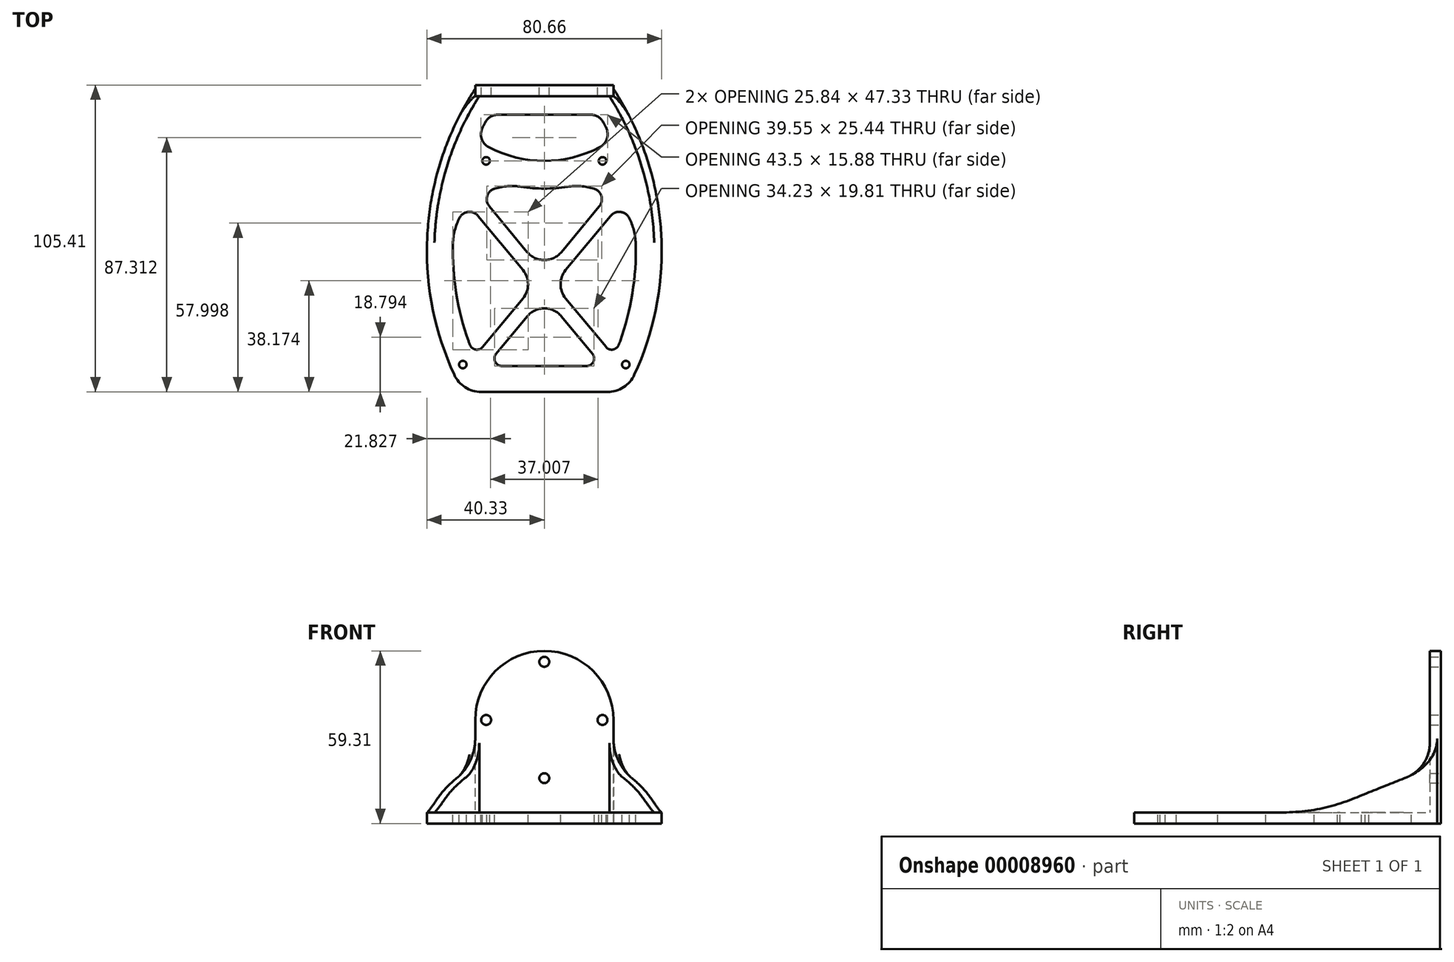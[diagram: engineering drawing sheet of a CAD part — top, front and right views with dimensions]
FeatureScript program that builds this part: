
annotation { "Feature Type Name" : "Feature", "Feature Type Description" : "" }
export const myFeature = defineFeature(function(context is Context, id is Id, definition is map)
    precondition{}
    {
        {
            var Q0;
            Q0=qCreatedBy(makeId("Front.planeOp"),FACE);
            var sketch = newSketch(context, id + "F0", { "sketchPlane" : qUnion([Q0])});
            skCircle(sketch, "E0", {"center": v(0, 19.99) * mm, "radius": 1.7 * mm});
            skCircle(sketch, "E1.1.0", {"center": v(-19.99, 0) * mm, "radius": 1.7 * mm});
            skCircle(sketch, "E1.2.0", {"center": v(0, -19.99) * mm, "radius": 1.7 * mm});
            skCircle(sketch, "E1.3.0", {"center": v(19.99, 0) * mm, "radius": 1.7 * mm});
            skPoint(sketch, "E1.center", {"position": v(0, 0) * mm});
            skArc(sketch, "E2", {"start": v(23.75, 0) * mm, "mid": v(0, 23.75) * mm, "end": v(-23.75, 0) * mm});
            skLineSegment(sketch, "E3.top", {"start": v(-23.75, -31.75) * mm, "end": v(23.75, -31.75) * mm});
            skLineSegment(sketch, "E3.left", {"start": v(-23.75, 0) * mm, "end": v(-23.75, -31.75) * mm});
            skLineSegment(sketch, "E3.right", {"start": v(23.75, 0) * mm, "end": v(23.75, -31.75) * mm});
            skSolve(sketch);
        }
        {
            var Q0;
            Q0=qSketchRegion(id+"F0",true);
            extrude(context, id + "F1", {"entities" : qUnion([Q0]), "depth" : 2.54 * mm});
        }
        {
            var Q0;
            Q0=makeQuery(id+"F1.opExtrude","SWEPT_FACE",FACE,{"disambiguationData":[OSD([sQuery(id+"F0.wireOp",EDGE,"E3.top")])]});
            var sketch = newSketch(context, id + "F2", { "sketchPlane" : qUnion([Q0])});
            skCircle(sketch, "E4", {"center": v(-20, 24.77) * mm, "radius": 1.3 * mm});
            skCircle(sketch, "E5", {"center": v(-28, 94.77) * mm, "radius": 1.3 * mm});
            skLineSegment(sketch, "E6", {"start": v(-20, 24.77) * mm, "end": v(-20, 0) * mm, "construction": true});
            skLineSegment(sketch, "E7", {"start": v(-28, 94.77) * mm, "end": v(-28, 0) * mm, "construction": true});
            skCircle(sketch, "E8.0.MirrorC", {"center": v(20, 24.77) * mm, "radius": 1.3 * mm});
            skCircle(sketch, "E8.1.MirrorC", {"center": v(28, 94.77) * mm, "radius": 1.3 * mm});
            skArc(sketch, "E9", {"start": v(-30.96, 98.24) * mm, "mid": v(-40.06, 48.19) * mm, "end": v(-23.75, 0) * mm});
            skArc(sketch, "E10.0.MirrorCS", {"start": v(30.96, 98.24) * mm, "mid": v(40.06, 48.19) * mm, "end": v(23.75, 0) * mm});
            skLineSegment(sketch, "E11", {"start": v(-21.74, 104.14) * mm, "end": v(21.74, 104.14) * mm});
            skPoint(sketch, "E12.visualSharp", {"position": v(-28, 104.14) * mm});
            skArc(sketch, "E12.filletArc", {"start": v(-21.74, 104.14) * mm, "mid": v(-27.22, 102.54) * mm, "end": v(-30.96, 98.24) * mm});
            skPoint(sketch, "E13.visualSharp", {"position": v(28, 104.14) * mm});
            skArc(sketch, "E13.filletArc", {"start": v(30.96, 98.24) * mm, "mid": v(27.22, 102.54) * mm, "end": v(21.74, 104.14) * mm});
            skLineSegment(sketch, "E14", {"start": v(-23.75, 0) * mm, "end": v(23.75, 0) * mm});
            skArc(sketch, "E15.0", {"start": v(-26.04, 86.82) * mm, "mid": v(-30.28, 70.26) * mm, "end": v(-31.41, 53.2) * mm});
            skLineSegment(sketch, "E15.1", {"start": v(-14.08, 95.25) * mm, "end": v(14.08, 95.25) * mm});
            skArc(sketch, "E15.2", {"start": v(26.04, 86.82) * mm, "mid": v(30.28, 70.26) * mm, "end": v(31.41, 53.2) * mm});
            skLineSegment(sketch, "E15.3", {"start": v(-15.83, 8.89) * mm, "end": v(15.83, 8.89) * mm});
            skArc(sketch, "E16", {"start": v(7.93, 33.67) * mm, "mid": v(0, 34.3) * mm, "end": v(-7.93, 33.67) * mm});
            skArc(sketch, "E17", {"start": v(19.03, 20.12) * mm, "mid": v(0, 24.77) * mm, "end": v(-19.03, 20.12) * mm});
            skArc(sketch, "E18.trimOffspring", {"start": v(21.2, 13.29) * mm, "mid": v(20.76, 12.42) * mm, "end": v(20.3, 11.55) * mm});
            skArc(sketch, "E19.trimOffspring", {"start": v(-21.2, 13.29) * mm, "mid": v(-20.76, 12.42) * mm, "end": v(-20.3, 11.55) * mm});
            skPoint(sketch, "E20.visualSharp", {"position": v(-26.8, 26.65) * mm});
            skArc(sketch, "E20.filletArc", {"start": v(-31.41, 53.2) * mm, "mid": v(-30.77, 48.64) * mm, "end": v(-29.1, 44.33) * mm});
            skPoint(sketch, "E21.visualSharp", {"position": v(26.8, 26.65) * mm});
            skArc(sketch, "E21.filletArc", {"start": v(7.93, 33.67) * mm, "mid": v(12.55, 33.47) * mm, "end": v(17.1, 34.32) * mm});
            skPoint(sketch, "E22.visualSharp", {"position": v(18.8, 8.89) * mm});
            skArc(sketch, "E22.filletArc", {"start": v(15.83, 8.89) * mm, "mid": v(18.43, 9.6) * mm, "end": v(20.3, 11.55) * mm});
            skPoint(sketch, "E23.visualSharp", {"position": v(-18.8, 8.89) * mm});
            skArc(sketch, "E23.filletArc", {"start": v(-20.3, 11.55) * mm, "mid": v(-18.43, 9.6) * mm, "end": v(-15.83, 8.89) * mm});
            skPoint(sketch, "E24.visualSharp", {"position": v(-23.27, 17.58) * mm});
            skArc(sketch, "E24.filletArc", {"start": v(-19.03, 20.12) * mm, "mid": v(-21.53, 17.15) * mm, "end": v(-21.2, 13.29) * mm});
            skPoint(sketch, "E25.visualSharp", {"position": v(23.27, 17.58) * mm});
            skArc(sketch, "E25.filletArc", {"start": v(21.2, 13.29) * mm, "mid": v(21.53, 17.15) * mm, "end": v(19.03, 20.12) * mm});
            skPoint(sketch, "E26.visualSharp", {"position": v(-22.55, 95.25) * mm});
            skArc(sketch, "E26.filletArc", {"start": v(-14.08, 95.25) * mm, "mid": v(-14.4, 95.25) * mm, "end": v(-14.73, 95.23) * mm});
            skPoint(sketch, "E27.visualSharp", {"position": v(22.55, 95.25) * mm});
            skArc(sketch, "E27.filletArc", {"start": v(26.04, 86.82) * mm, "mid": v(25.76, 87.54) * mm, "end": v(25.43, 88.24) * mm});
            skLineSegment(sketch, "E28", {"start": v(-21.4, 92.93) * mm, "end": v(24.1, 38.12) * mm, "construction": true});
            skLineSegment(sketch, "E29", {"start": v(-24.1, 38.12) * mm, "end": v(21.4, 92.93) * mm, "construction": true});
            skLineSegment(sketch, "E30.0", {"start": v(-21.2, 88.73) * mm, "end": v(-7.34, 72.02) * mm});
            skLineSegment(sketch, "E31.0", {"start": v(-16.55, 91.07) * mm, "end": v(-5.86, 78.2) * mm});
            skLineSegment(sketch, "E32.0", {"start": v(-18.9, 40.4) * mm, "end": v(-5.86, 56.1) * mm});
            skLineSegment(sketch, "E33.0", {"start": v(-22.8, 43.66) * mm, "end": v(-7.34, 62.29) * mm});
            skArc(sketch, "E34.trimOffspring", {"start": v(14.73, 95.23) * mm, "mid": v(14.4, 95.25) * mm, "end": v(14.08, 95.25) * mm});
            skArc(sketch, "E35.trimOffspring", {"start": v(-25.43, 88.24) * mm, "mid": v(-25.76, 87.54) * mm, "end": v(-26.04, 86.82) * mm});
            skLineSegment(sketch, "E36.trimOffspring", {"start": v(5.86, 78.2) * mm, "end": v(16.55, 91.07) * mm});
            skLineSegment(sketch, "E37.trimOffspring", {"start": v(7.34, 62.29) * mm, "end": v(22.8, 43.66) * mm});
            skLineSegment(sketch, "E38.trimOffspring", {"start": v(7.34, 72.02) * mm, "end": v(21.2, 88.73) * mm});
            skLineSegment(sketch, "E39.trimOffspring", {"start": v(5.86, 56.1) * mm, "end": v(18.9, 40.4) * mm});
            skArc(sketch, "E40.trimOffspring", {"start": v(-17.1, 34.32) * mm, "mid": v(-12.55, 33.47) * mm, "end": v(-7.93, 33.67) * mm});
            skArc(sketch, "E41.trimOffspring", {"start": v(29.1, 44.33) * mm, "mid": v(30.77, 48.64) * mm, "end": v(31.41, 53.2) * mm});
            skPoint(sketch, "E42.visualSharp", {"position": v(-3.3, 67.15) * mm});
            skArc(sketch, "E42.filletArc", {"start": v(-7.34, 62.29) * mm, "mid": v(-5.58, 67.15) * mm, "end": v(-7.34, 72.02) * mm});
            skPoint(sketch, "E43.visualSharp", {"position": v(3.3, 67.15) * mm});
            skArc(sketch, "E43.filletArc", {"start": v(7.34, 72.02) * mm, "mid": v(5.58, 67.15) * mm, "end": v(7.34, 62.29) * mm});
            skPoint(sketch, "E44.visualSharp", {"position": v(0, 71.13) * mm});
            skArc(sketch, "E44.filletArc", {"start": v(-5.86, 78.2) * mm, "mid": v(0, 75.44) * mm, "end": v(5.86, 78.2) * mm});
            skPoint(sketch, "E45.visualSharp", {"position": v(0, 63.18) * mm});
            skArc(sketch, "E45.filletArc", {"start": v(5.86, 56.1) * mm, "mid": v(0, 58.86) * mm, "end": v(-5.86, 56.1) * mm});
            skPoint(sketch, "E46.visualSharp", {"position": v(25.95, 39.87) * mm});
            skArc(sketch, "E46.filletArc", {"start": v(22.8, 43.66) * mm, "mid": v(26.13, 42.3) * mm, "end": v(29.1, 44.33) * mm});
            skPoint(sketch, "E47.visualSharp", {"position": v(22.04, 36.62) * mm});
            skArc(sketch, "E47.filletArc", {"start": v(17.1, 34.32) * mm, "mid": v(19.62, 36.88) * mm, "end": v(18.9, 40.4) * mm});
            skPoint(sketch, "E48.visualSharp", {"position": v(-22.04, 36.62) * mm});
            skArc(sketch, "E48.filletArc", {"start": v(-18.9, 40.4) * mm, "mid": v(-19.62, 36.88) * mm, "end": v(-17.1, 34.32) * mm});
            skPoint(sketch, "E49.visualSharp", {"position": v(-25.95, 39.87) * mm});
            skArc(sketch, "E49.filletArc", {"start": v(-29.1, 44.33) * mm, "mid": v(-26.13, 42.3) * mm, "end": v(-22.8, 43.66) * mm});
            skPoint(sketch, "E50.visualSharp", {"position": v(19.14, 94.2) * mm});
            skArc(sketch, "E50.filletArc", {"start": v(16.55, 91.07) * mm, "mid": v(16.92, 93.72) * mm, "end": v(14.73, 95.23) * mm});
            skPoint(sketch, "E51.visualSharp", {"position": v(23.31, 91.27) * mm});
            skArc(sketch, "E51.filletArc", {"start": v(25.43, 88.24) * mm, "mid": v(23.45, 89.63) * mm, "end": v(21.2, 88.73) * mm});
            skPoint(sketch, "E52.visualSharp", {"position": v(-19.14, 94.2) * mm});
            skArc(sketch, "E52.filletArc", {"start": v(-14.73, 95.23) * mm, "mid": v(-16.92, 93.72) * mm, "end": v(-16.55, 91.07) * mm});
            skPoint(sketch, "E53.visualSharp", {"position": v(-23.31, 91.27) * mm});
            skArc(sketch, "E53.filletArc", {"start": v(-21.2, 88.73) * mm, "mid": v(-23.45, 89.63) * mm, "end": v(-25.43, 88.24) * mm});
            skSolve(sketch);
        }
        {
            var Q0;
            Q0=qSketchRegion(id+"F2",true);
            extrude(context, id + "F3", {"entities" : qUnion([Q0]), "operationType" : NewBodyOperationType.ADD, "depth" : 3.8 * mm});
        }
        {
            var Q0;
            Q0=makeQuery(id+"F3.opExtrude","CAP_FACE",FACE,{"disambiguationData":[OSD([sQuery(id+"F2.wireOp",EDGE,"E4"),sQuery(id+"F2.wireOp",EDGE,"E5"),sQuery(id+"F2.wireOp",EDGE,"E8.0.MirrorC"),sQuery(id+"F2.wireOp",EDGE,"E8.1.MirrorC"),sQuery(id+"F2.wireOp",EDGE,"E9"),sQuery(id+"F2.wireOp",EDGE,"E10.0.MirrorCS"),sQuery(id+"F2.wireOp",EDGE,"E11"),sQuery(id+"F2.wireOp",EDGE,"E12.filletArc"),sQuery(id+"F2.wireOp",EDGE,"E13.filletArc"),sQuery(id+"F2.wireOp",EDGE,"E14"),sQuery(id+"F2.wireOp",EDGE,"E15.0"),sQuery(id+"F2.wireOp",EDGE,"E15.1"),sQuery(id+"F2.wireOp",EDGE,"E15.2"),sQuery(id+"F2.wireOp",EDGE,"E15.3"),sQuery(id+"F2.wireOp",EDGE,"E16"),sQuery(id+"F2.wireOp",EDGE,"E17"),sQuery(id+"F2.wireOp",EDGE,"E18.trimOffspring"),sQuery(id+"F2.wireOp",EDGE,"E19.trimOffspring"),sQuery(id+"F2.wireOp",EDGE,"E20.filletArc"),sQuery(id+"F2.wireOp",EDGE,"E21.filletArc"),sQuery(id+"F2.wireOp",EDGE,"E22.filletArc"),sQuery(id+"F2.wireOp",EDGE,"E23.filletArc"),sQuery(id+"F2.wireOp",EDGE,"E24.filletArc"),sQuery(id+"F2.wireOp",EDGE,"E25.filletArc"),sQuery(id+"F2.wireOp",EDGE,"E26.filletArc"),sQuery(id+"F2.wireOp",EDGE,"E27.filletArc"),sQuery(id+"F2.wireOp",EDGE,"E30.0"),sQuery(id+"F2.wireOp",EDGE,"E31.0"),sQuery(id+"F2.wireOp",EDGE,"E32.0"),sQuery(id+"F2.wireOp",EDGE,"E33.0"),sQuery(id+"F2.wireOp",EDGE,"E34.trimOffspring"),sQuery(id+"F2.wireOp",EDGE,"E35.trimOffspring"),sQuery(id+"F2.wireOp",EDGE,"E36.trimOffspring"),sQuery(id+"F2.wireOp",EDGE,"E37.trimOffspring"),sQuery(id+"F2.wireOp",EDGE,"E38.trimOffspring"),sQuery(id+"F2.wireOp",EDGE,"E39.trimOffspring"),sQuery(id+"F2.wireOp",EDGE,"E40.trimOffspring"),sQuery(id+"F2.wireOp",EDGE,"E41.trimOffspring"),sQuery(id+"F2.wireOp",EDGE,"E42.filletArc"),sQuery(id+"F2.wireOp",EDGE,"E43.filletArc"),sQuery(id+"F2.wireOp",EDGE,"E44.filletArc"),sQuery(id+"F2.wireOp",EDGE,"E45.filletArc"),sQuery(id+"F2.wireOp",EDGE,"E46.filletArc"),sQuery(id+"F2.wireOp",EDGE,"E47.filletArc"),sQuery(id+"F2.wireOp",EDGE,"E48.filletArc"),sQuery(id+"F2.wireOp",EDGE,"E49.filletArc"),sQuery(id+"F2.wireOp",EDGE,"E50.filletArc"),sQuery(id+"F2.wireOp",EDGE,"E51.filletArc"),sQuery(id+"F2.wireOp",EDGE,"E52.filletArc"),sQuery(id+"F2.wireOp",EDGE,"E53.filletArc")])],"isStart":true});
            var sketch = newSketch(context, id + "F4", { "sketchPlane" : qUnion([Q0])});
            skArc(sketch, "E54.0", {"start": v(-40.33, -55.63) * mm, "mid": v(-36.1, -26.6) * mm, "end": v(-23.75, 0) * mm});
            skArc(sketch, "E55.0", {"start": v(-37.8, -55.63) * mm, "mid": v(-33.66, -27.33) * mm, "end": v(-21.62, -1.4) * mm});
            skLineSegment(sketch, "E56", {"start": v(-40.33, -55.63) * mm, "end": v(-37.8, -55.63) * mm});
            skPoint(sketch, "E57.orphan", {"position": v(-30.96, -98.24) * mm});
            skLineSegment(sketch, "E58", {"start": v(-23.75, 0) * mm, "end": v(-21.62, -1.4) * mm});
            skLineSegment(sketch, "E59.0.MirrorCS", {"start": v(40.33, -55.63) * mm, "end": v(37.8, -55.63) * mm});
            skLineSegment(sketch, "E59.1.MirrorCS", {"start": v(23.75, 0) * mm, "end": v(21.62, -1.4) * mm});
            skArc(sketch, "E59.2.MirrorCS", {"start": v(37.8, -55.63) * mm, "mid": v(33.66, -27.33) * mm, "end": v(21.62, -1.4) * mm});
            skArc(sketch, "E59.3.MirrorCS", {"start": v(40.33, -55.63) * mm, "mid": v(36.1, -26.6) * mm, "end": v(23.75, 0) * mm});
            skSolve(sketch);
        }
        {
            var Q0;
            Q0=qSketchRegion(id+"F4",true);
            extrude(context, id + "F5", {"entities" : qUnion([Q0]), "operationType" : NewBodyOperationType.ADD, "depth" : 25.4 * mm});
        }
        {
            var Q0;
            Q0=qCreatedBy(makeId("Right.planeOp"),FACE);
            cPlane(context, id + "F6", {"entities" : qUnion([Q0]), "cplaneType" : CPlaneType.OFFSET, "offset" : 152.4 * mm, "width" : 152.4 * mm, "height" : 152.4 * mm});
        }
        {
            var Q0;
            Q0=qCreatedBy(id+"F6.planeOp",FACE);
            var sketch = newSketch(context, id + "F7", { "sketchPlane" : qUnion([Q0])});
            skPoint(sketch, "E60.orphan", {"position": v(0, -6.35) * mm});
            skPoint(sketch, "E61.0.end.orphan", {"position": v(-55.63, -6.35) * mm});
            skLineSegment(sketch, "E62", {"start": v(-55.63, -31.75) * mm, "end": v(-52.87, -31.75) * mm});
            skPoint(sketch, "E61.3.start.orphan", {"position": v(-2.54, 0) * mm});
            skLineSegment(sketch, "E63", {"start": v(-2.54, -6.35) * mm, "end": v(-55.63, -6.35) * mm});
            skPoint(sketch, "E61.2.end.orphan", {"position": v(-98.24, -31.75) * mm});
            skLineSegment(sketch, "E64", {"start": v(-55.63, -31.75) * mm, "end": v(-55.63, -6.35) * mm});
            skLineSegment(sketch, "E65", {"start": v(-29.29, -27.2) * mm, "end": v(-10.52, -19.7) * mm});
            skLineSegment(sketch, "E66", {"start": v(-2.54, -6.35) * mm, "end": v(-2.54, -7.91) * mm});
            skPoint(sketch, "E67.start.orphan", {"position": v(-2.54, -31.75) * mm});
            skPoint(sketch, "E68.orphan", {"position": v(-25.65, -31.75) * mm});
            skPoint(sketch, "E69.visualSharp", {"position": v(-2.54, -16.5) * mm});
            skArc(sketch, "E69.filletArc", {"start": v(-10.52, -19.7) * mm, "mid": v(-4.72, -15.03) * mm, "end": v(-2.54, -7.91) * mm});
            skPoint(sketch, "E70.visualSharp", {"position": v(-40.64, -31.75) * mm});
            skArc(sketch, "E70.filletArc", {"start": v(-52.87, -31.75) * mm, "mid": v(-40.86, -30.6) * mm, "end": v(-29.29, -27.2) * mm});
            skSolve(sketch);
        }
        {
            var Q0;
            Q0=qSketchRegion(id+"F7",true);
            extrude(context, id + "F8", {"entities" : qUnion([Q0]), "operationType" : NewBodyOperationType.REMOVE, "endBound" : BoundingType.THROUGH_ALL, "oppositeDirection" : true, "depth" : 25.4 * mm});
        }
        {
            var Q0;
            Q0=makeQuery(id+"F3.boolean.opBoolean","MERGE",FACE,{"derivedFrom":[makeQuery(id+"F1.opExtrude","CAP_FACE",FACE,{"disambiguationData":[OSD([sQuery(id+"F0.wireOp",EDGE,"E0"),sQuery(id+"F0.wireOp",EDGE,"E1.1.0"),sQuery(id+"F0.wireOp",EDGE,"E1.2.0"),sQuery(id+"F0.wireOp",EDGE,"E1.3.0"),sQuery(id+"F0.wireOp",EDGE,"E2"),sQuery(id+"F0.wireOp",EDGE,"E3.top"),sQuery(id+"F0.wireOp",EDGE,"E3.left"),sQuery(id+"F0.wireOp",EDGE,"E3.right")])],"isStart":true}),makeQuery(id+"F3.opExtrude","SWEPT_FACE",FACE,{"disambiguationData":[OSD([sQuery(id+"F2.wireOp",EDGE,"E14")])]})]});
            var sketch = newSketch(context, id + "F9", { "sketchPlane" : qUnion([Q0])});
            skFitSpline(sketch, "E71.0", {"points": [v(29.77, -19.7) * mm, v(29.5, -19.48) * mm, v(29.22, -19.22) * mm, v(28.95, -18.91) * mm, v(28.67, -18.61) * mm, v(28.4, -18.27) * mm, v(28.15, -17.9) * mm, v(27.9, -17.52) * mm, v(27.64, -17.1) * mm, v(27.4, -16.66) * mm, v(27.16, -16.2) * mm, v(26.94, -15.73) * mm, v(26.74, -15.23) * mm, v(26.52, -14.7) * mm, v(26.33, -14.16) * mm, v(26.17, -13.6) * mm, v(26, -13.01) * mm, v(25.85, -12.42) * mm, v(25.73, -11.8) * mm, v(25.6, -11.18) * mm, v(25.52, -10.55) * mm, v(25.45, -9.9) * mm, v(25.39, -9.24) * mm, v(25.36, -8.58) * mm, v(25.36, -7.91) * mm]});
            skLineSegment(sketch, "E71.1", {"start": v(25.36, -6.35) * mm, "end": v(25.36, -7.91) * mm});
            skFitSpline(sketch, "E71.6.3", {"points": [v(29.77, -19.7) * mm, v(29.5, -19.48) * mm, v(29.22, -19.22) * mm, v(28.95, -18.91) * mm, v(28.67, -18.61) * mm, v(28.4, -18.27) * mm, v(28.15, -17.9) * mm, v(27.9, -17.52) * mm, v(27.64, -17.1) * mm, v(27.4, -16.66) * mm, v(27.16, -16.2) * mm, v(26.94, -15.73) * mm, v(26.74, -15.23) * mm, v(26.52, -14.7) * mm, v(26.33, -14.16) * mm, v(26.17, -13.6) * mm, v(26, -13.01) * mm, v(25.85, -12.42) * mm, v(25.73, -11.8) * mm, v(25.6, -11.18) * mm, v(25.52, -10.55) * mm, v(25.45, -9.9) * mm, v(25.39, -9.24) * mm, v(25.36, -8.58) * mm, v(25.36, -7.91) * mm]});
            skLineSegment(sketch, "E71.6.4", {"start": v(25.36, -6.35) * mm, "end": v(25.36, -7.91) * mm});
            skArc(sketch, "E72", {"start": v(23.75, -6.35) * mm, "mid": v(25.32, -13.67) * mm, "end": v(29.77, -19.7) * mm});
            skLineSegment(sketch, "E73", {"start": v(23.75, -6.35) * mm, "end": v(25.36, -6.35) * mm});
            skLineSegment(sketch, "E74.0.MirrorCS", {"start": v(-23.75, -6.35) * mm, "end": v(-25.36, -6.35) * mm});
            skArc(sketch, "E75.0.MirrorCS", {"start": v(-23.75, -6.35) * mm, "mid": v(-25.32, -13.67) * mm, "end": v(-29.77, -19.7) * mm});
            skFitSpline(sketch, "E76.0.MirrorCS", {"points": [v(-29.77, -19.7) * mm, v(-29.5, -19.48) * mm, v(-29.22, -19.22) * mm, v(-28.95, -18.91) * mm, v(-28.67, -18.61) * mm, v(-28.4, -18.27) * mm, v(-28.15, -17.9) * mm, v(-27.9, -17.52) * mm, v(-27.64, -17.1) * mm, v(-27.4, -16.66) * mm, v(-27.16, -16.2) * mm, v(-26.94, -15.73) * mm, v(-26.74, -15.23) * mm, v(-26.52, -14.7) * mm, v(-26.33, -14.16) * mm, v(-26.17, -13.6) * mm, v(-26, -13.01) * mm, v(-25.85, -12.42) * mm, v(-25.73, -11.8) * mm, v(-25.6, -11.18) * mm, v(-25.52, -10.55) * mm, v(-25.45, -9.9) * mm, v(-25.39, -9.24) * mm, v(-25.36, -8.58) * mm, v(-25.36, -7.91) * mm]});
            skLineSegment(sketch, "E77.0.MirrorCS", {"start": v(-25.36, -6.35) * mm, "end": v(-25.36, -7.91) * mm});
            skSolve(sketch);
        }
        {
            var Q0;
            Q0=qSketchRegion(id+"F9",true);
            extrude(context, id + "F10", {"entities" : qUnion([Q0]), "operationType" : NewBodyOperationType.REMOVE, "endBound" : BoundingType.THROUGH_ALL, "oppositeDirection" : true, "depth" : 25.4 * mm});
        }
        {
            var Q0;
            Q0=makeQuery(id+"F3.boolean.opBoolean","MERGE",FACE,{"derivedFrom":[makeQuery(id+"F1.opExtrude","CAP_FACE",FACE,{"disambiguationData":[OSD([sQuery(id+"F0.wireOp",EDGE,"E0"),sQuery(id+"F0.wireOp",EDGE,"E1.1.0"),sQuery(id+"F0.wireOp",EDGE,"E1.2.0"),sQuery(id+"F0.wireOp",EDGE,"E1.3.0"),sQuery(id+"F0.wireOp",EDGE,"E2"),sQuery(id+"F0.wireOp",EDGE,"E3.top"),sQuery(id+"F0.wireOp",EDGE,"E3.left"),sQuery(id+"F0.wireOp",EDGE,"E3.right")])],"isStart":true}),makeQuery(id+"F3.opExtrude","SWEPT_FACE",FACE,{"disambiguationData":[OSD([sQuery(id+"F2.wireOp",EDGE,"E14")])]})]});
            var sketch = newSketch(context, id + "F11", { "sketchPlane" : qUnion([Q0])});
            skArc(sketch, "E78.0", {"start": v(-23.75, 0) * mm, "mid": v(0, 23.75) * mm, "end": v(23.75, 0) * mm});
            skLineSegment(sketch, "E78.1", {"start": v(-23.75, -35.56) * mm, "end": v(-23.75, -6.35) * mm});
            skLineSegment(sketch, "E78.2", {"start": v(-23.75, 0) * mm, "end": v(-23.75, -6.35) * mm});
            skLineSegment(sketch, "E78.3", {"start": v(23.75, 0) * mm, "end": v(23.75, -6.35) * mm});
            skLineSegment(sketch, "E78.4", {"start": v(23.75, -35.56) * mm, "end": v(23.75, -6.35) * mm});
            skLineSegment(sketch, "E78.5", {"start": v(23.75, -35.56) * mm, "end": v(-23.75, -35.56) * mm});
            skCircle(sketch, "E78.6", {"center": v(0, -19.99) * mm, "radius": 1.7 * mm});
            skCircle(sketch, "E78.7", {"center": v(19.99, 0) * mm, "radius": 1.7 * mm});
            skCircle(sketch, "E78.8", {"center": v(0, 19.99) * mm, "radius": 1.7 * mm});
            skCircle(sketch, "E78.9", {"center": v(-19.99, 0) * mm, "radius": 1.7 * mm});
            skSolve(sketch);
        }
        {
            var Q0;
            Q0=qSketchRegion(id+"F11",true);
            extrude(context, id + "F12", {"entities" : qUnion([Q0]), "operationType" : NewBodyOperationType.ADD, "depth" : 1.27 * mm});
        }
    });
